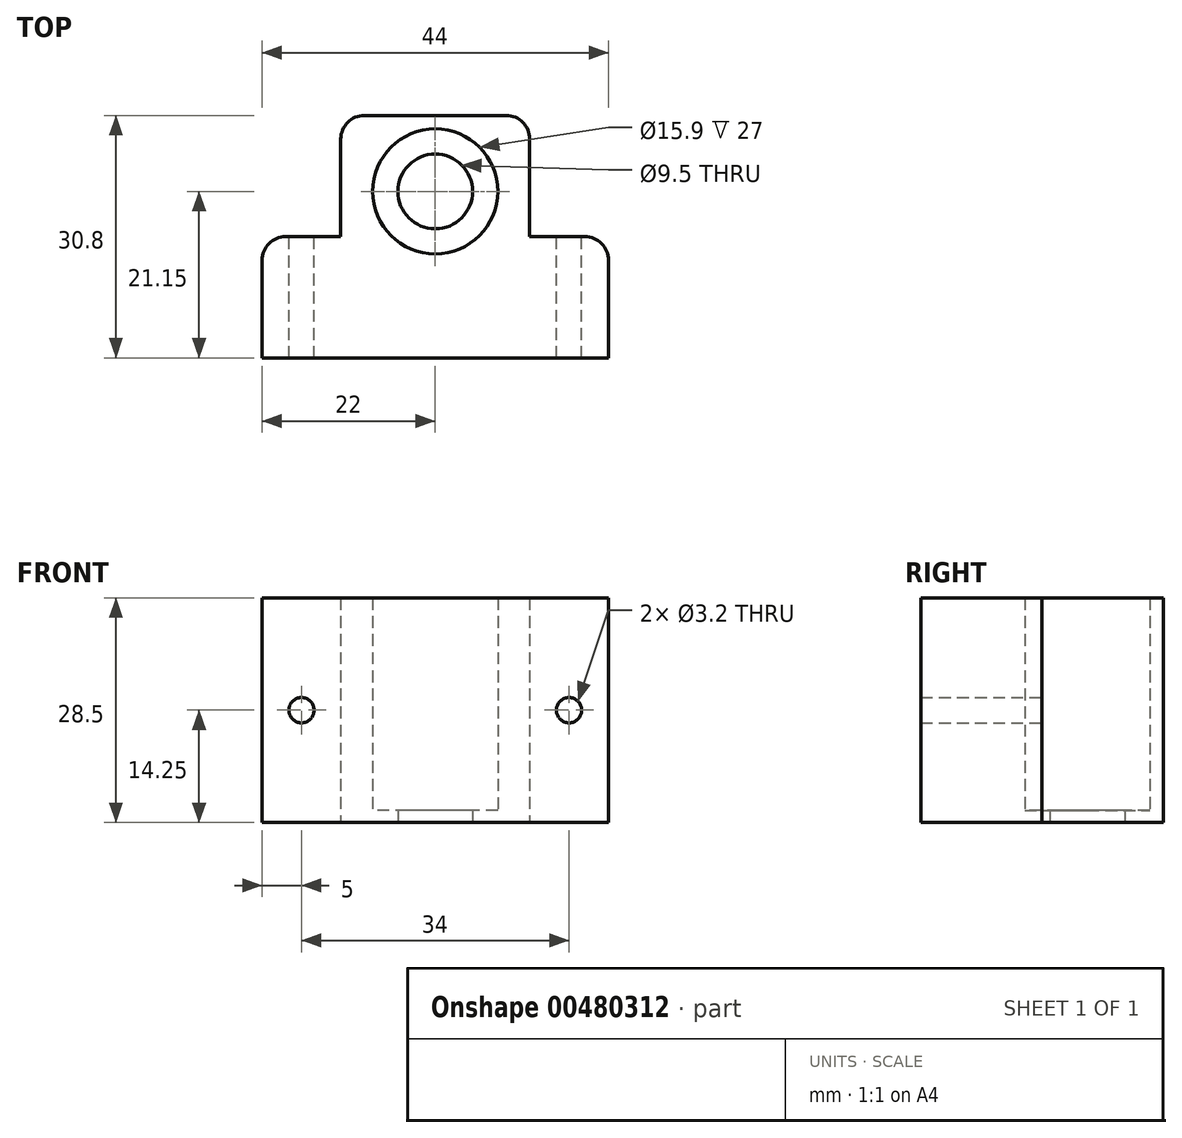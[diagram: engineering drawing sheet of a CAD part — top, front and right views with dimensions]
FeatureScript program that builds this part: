
annotation { "Feature Type Name" : "Feature", "Feature Type Description" : "" }
export const myFeature = defineFeature(function(context is Context, id is Id, definition is map)
    precondition{}
    {
        {
            var Q0;
            Q0=qCreatedBy(makeId("Top.planeOp"),FACE);
            var sketch = newSketch(context, id + "F0", { "sketchPlane" : qUnion([Q0])});
            skLineSegment(sketch, "E0.bottom", {"start": v(-12, -15.4) * mm, "end": v(12, -15.4) * mm});
            skLineSegment(sketch, "E0.top", {"start": v(-12, 15.4) * mm, "end": v(12, 15.4) * mm});
            skLineSegment(sketch, "E0.left", {"start": v(-12, -15.4) * mm, "end": v(-12, 15.4) * mm});
            skLineSegment(sketch, "E0.right", {"start": v(12, -15.4) * mm, "end": v(12, 15.4) * mm});
            skPoint(sketch, "E0.middle", {"position": v(0, 0) * mm});
            skCircle(sketch, "E1", {"center": v(0, 5.75) * mm, "radius": 4.75 * mm});
            skCircle(sketch, "E2.0", {"center": v(0, 5.75) * mm, "radius": 7.95 * mm});
            skSolve(sketch);
        }
        {
            var Q0;
            Q0=makeQuery(id+"F0.imprint","IMPRINT",FACE,{"disambiguationData":[TD([[makeQuery(id+"F0.imprint","IMPRINT",EDGE,{"derivedFrom":sQuery(id+"F0.wireOp",EDGE,"E0.bottom")}),1.0]])]});
            extrude(context, id + "F1", {"entities" : qUnion([Q0]), "depth" : 28.5 * mm});
        }
        {
            var Q0;
            Q0=makeQuery(id+"F1.opExtrude","SWEPT_FACE",FACE,{"disambiguationData":[OSD([sQuery(id+"F0.wireOp",EDGE,"E0.left")])]});
            var sketch = newSketch(context, id + "F2", { "sketchPlane" : qUnion([Q0])});
            skLineSegment(sketch, "E3.0", {"start": v(15.4, 28.5) * mm, "end": v(15.4, 0) * mm});
            skLineSegment(sketch, "E4.bottom", {"start": v(15.4, 0) * mm, "end": v(0, 0) * mm});
            skLineSegment(sketch, "E4.top", {"start": v(15.4, 28.5) * mm, "end": v(0, 28.5) * mm});
            skLineSegment(sketch, "E4.left", {"start": v(15.4, 0) * mm, "end": v(15.4, 28.5) * mm});
            skLineSegment(sketch, "E4.right", {"start": v(0, 0) * mm, "end": v(0, 28.5) * mm});
            skSolve(sketch);
        }
        {
            var Q0;
            Q0=makeQuery(id+"F1.opExtrude","SWEPT_FACE",FACE,{"disambiguationData":[OSD([sQuery(id+"F0.wireOp",EDGE,"E0.right")])]});
            var sketch = newSketch(context, id + "F3", { "sketchPlane" : qUnion([Q0])});
            skLineSegment(sketch, "E5.0", {"start": v(0, 0) * mm, "end": v(0, 28.5) * mm});
            skLineSegment(sketch, "E6.0", {"start": v(-15.4, 0) * mm, "end": v(-15.4, 28.5) * mm});
            skLineSegment(sketch, "E7.bottom", {"start": v(-15.4, 28.5) * mm, "end": v(0, 28.5) * mm});
            skLineSegment(sketch, "E7.top", {"start": v(-15.4, 28.5) * mm, "end": v(0, 28.5) * mm});
            skLineSegment(sketch, "E7.left", {"start": v(-15.4, 28.5) * mm, "end": v(-15.4, 28.5) * mm});
            skLineSegment(sketch, "E7.right", {"start": v(0, 28.5) * mm, "end": v(0, 28.5) * mm});
            skLineSegment(sketch, "E8.bottom", {"start": v(-15.4, 0) * mm, "end": v(0, 0) * mm});
            skCircle(sketch, "E9", {"center": v(0, 28.5) * mm, "radius": 52.6 * mm});
            skSolve(sketch);
        }
        {
            var Q0;
            Q0=makeQuery(id+"F3.imprint","IMPRINT",FACE,{"disambiguationData":[TD([[makeQuery(id+"F3.imprint","IMPRINT",EDGE,{"derivedFrom":sQuery(id+"F3.wireOp",EDGE,"E8.bottom")}),1.0]])]});
            extrude(context, id + "F4", {"entities" : qUnion([Q0]), "operationType" : NewBodyOperationType.ADD, "depth" : 10 * mm});
        }
        {
            var Q0;
            Q0=makeQuery(id+"F2.imprint","IMPRINT",FACE,{"disambiguationData":[TD([[makeQuery(id+"F2.imprint","IMPRINT",EDGE,{"derivedFrom":sQuery(id+"F2.wireOp",EDGE,"E4.bottom")}),-1.0]])]});
            extrude(context, id + "F5", {"entities" : qUnion([Q0]), "operationType" : NewBodyOperationType.ADD, "depth" : 10 * mm});
        }
        {
            var Q0;
            Q0=makeQuery(id+"F1.opExtrude","SWEPT_FACE",FACE,{"disambiguationData":[OSD([sQuery(id+"F0.wireOp",EDGE,"E0.top")])]});
            var sketch = newSketch(context, id + "F6", { "sketchPlane" : qUnion([Q0])});
            skLineSegment(sketch, "E10.0", {"start": v(22, 0) * mm, "end": v(22, 28.5) * mm});
            skLineSegment(sketch, "E10.1", {"start": v(-22, 0) * mm, "end": v(-22, 28.5) * mm});
            skLineSegment(sketch, "E10.2", {"start": v(-12, 28.5) * mm, "end": v(-12, 0) * mm});
            skLineSegment(sketch, "E10.3", {"start": v(12, 28.5) * mm, "end": v(12, 0) * mm});
            skLineSegment(sketch, "E11.0", {"start": v(-22, 28.5) * mm, "end": v(-12, 28.5) * mm});
            skLineSegment(sketch, "E11.1", {"start": v(22, 28.5) * mm, "end": v(12, 28.5) * mm});
            skLineSegment(sketch, "E11.2", {"start": v(22, 0) * mm, "end": v(12, 0) * mm});
            skLineSegment(sketch, "E11.3", {"start": v(-22, 0) * mm, "end": v(-12, 0) * mm});
            skLineSegment(sketch, "E12", {"start": v(17, 28.5) * mm, "end": v(17, 0) * mm, "construction": true});
            skLineSegment(sketch, "E13", {"start": v(12, 14.25) * mm, "end": v(22, 14.25) * mm, "construction": true});
            skLineSegment(sketch, "E14", {"start": v(-22, 14.25) * mm, "end": v(-12, 14.25) * mm, "construction": true});
            skLineSegment(sketch, "E15", {"start": v(-17, 28.5) * mm, "end": v(-17, 0) * mm, "construction": true});
            skCircle(sketch, "E16", {"center": v(-17, 14.25) * mm, "radius": 1.6 * mm});
            skCircle(sketch, "E17", {"center": v(17, 14.25) * mm, "radius": 1.6 * mm});
            skSolve(sketch);
        }
        {
            var Q0;
            Q0=makeQuery(id+"F6.imprint","IMPRINT",FACE,{"disambiguationData":[TD([[makeQuery(id+"F6.imprint","IMPRINT",EDGE,{"derivedFrom":sQuery(id+"F6.wireOp",EDGE,"E16")}),1.0]])]});
            var Q1;
            Q1=makeQuery(id+"F6.imprint","IMPRINT",FACE,{"disambiguationData":[TD([[makeQuery(id+"F6.imprint","IMPRINT",EDGE,{"derivedFrom":sQuery(id+"F6.wireOp",EDGE,"E17")}),1.0]])]});
            extrude(context, id + "F7", {"entities" : qUnion([Q0, Q1]), "operationType" : NewBodyOperationType.REMOVE, "endBound" : BoundingType.THROUGH_ALL, "oppositeDirection" : true, "depth" : 25 * mm});
        }
        {
            var Q0;
            Q0=makeQuery(id+"F0.imprint","IMPRINT",FACE,{"disambiguationData":[TD([[makeQuery(id+"F0.imprint","IMPRINT",EDGE,{"derivedFrom":sQuery(id+"F0.wireOp",EDGE,"E1")}),-1.0]])]});
            extrude(context, id + "F8", {"entities" : qUnion([Q0]), "operationType" : NewBodyOperationType.ADD, "depth" : 1.5 * mm, "offsetDistance" : 25 * mm});
        }
        {
            var Q0;
            Q0=makeQuery(id+"F1.opExtrude","SWEPT_EDGE",EDGE,{"disambiguationData":[OSD([sQuery(id+"F0.wireOp",EDGE,"E0.top"),sQuery(id+"F0.wireOp",EDGE,"E0.right")])]});
            var Q1;
            Q1=makeQuery(id+"F4.opExtrude","CAP_EDGE",EDGE,{"disambiguationData":[OSD([sQuery(id+"F3.wireOp",EDGE,"E5.0")])],"isStart":false});
            var Q2;
            Q2=makeQuery(id+"F5.opExtrude","CAP_EDGE",EDGE,{"disambiguationData":[OSD([sQuery(id+"F2.wireOp",EDGE,"E4.right")])],"isStart":false});
            var Q3;
            Q3=makeQuery(id+"F1.opExtrude","SWEPT_EDGE",EDGE,{"disambiguationData":[OSD([sQuery(id+"F0.wireOp",EDGE,"E0.top"),sQuery(id+"F0.wireOp",EDGE,"E0.left")])]});
            fillet(context, id + "F9", {"entities" : qUnion([Q0, Q1, Q2, Q3]), "radius" : 3 * mm, "tangentPropagation" : true, "allowEdgeOverflow" : false});
        }
    });
